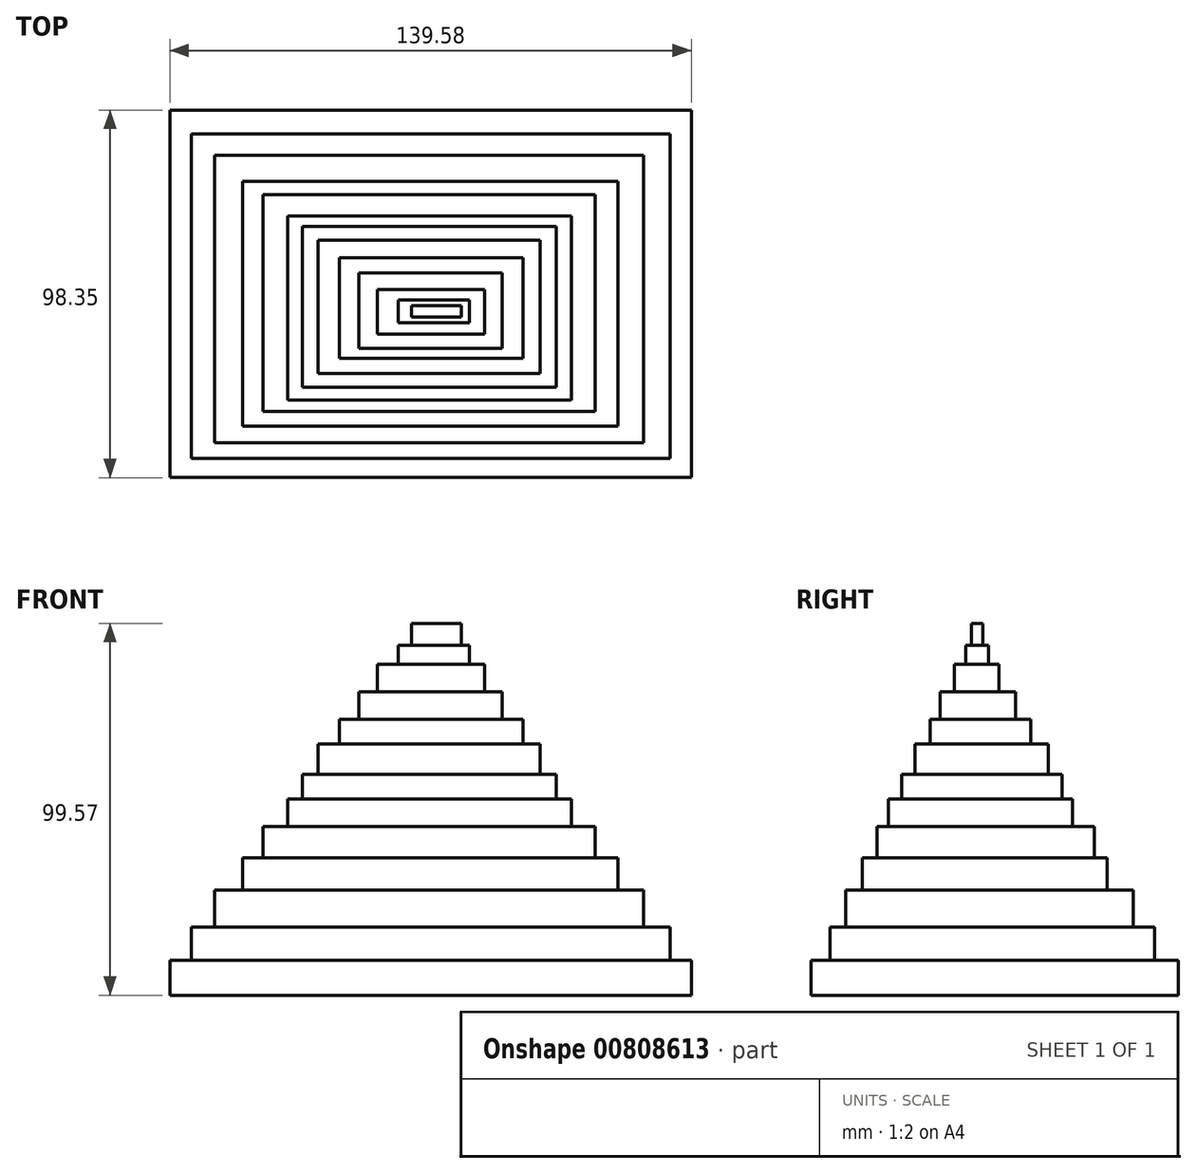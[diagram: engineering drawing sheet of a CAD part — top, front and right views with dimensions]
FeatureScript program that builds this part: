
annotation { "Feature Type Name" : "Feature", "Feature Type Description" : "" }
export const myFeature = defineFeature(function(context is Context, id is Id, definition is map)
    precondition{}
    {
        {
            var Q0;
            Q0=qCreatedBy(makeId("Top.planeOp"),FACE);
            var sketch = newSketch(context, id + "F0", { "sketchPlane" : qUnion([Q0])});
            skLineSegment(sketch, "E0.bottom", {"start": v(-69.6, 48.03) * mm, "end": v(69.98, 48.03) * mm});
            skLineSegment(sketch, "E0.top", {"start": v(-69.6, -50.32) * mm, "end": v(69.98, -50.32) * mm});
            skLineSegment(sketch, "E0.left", {"start": v(-69.6, 48.03) * mm, "end": v(-69.6, -50.32) * mm});
            skLineSegment(sketch, "E0.right", {"start": v(69.98, 48.03) * mm, "end": v(69.98, -50.32) * mm});
            skLineSegment(sketch, "E1.bottom", {"start": v(-63.87, 41.72) * mm, "end": v(64.26, 41.72) * mm});
            skLineSegment(sketch, "E1.top", {"start": v(-63.87, -45.16) * mm, "end": v(64.26, -45.16) * mm});
            skLineSegment(sketch, "E1.left", {"start": v(-63.87, 41.72) * mm, "end": v(-63.87, -45.16) * mm});
            skLineSegment(sketch, "E1.right", {"start": v(64.26, 41.72) * mm, "end": v(64.26, -45.16) * mm});
            skLineSegment(sketch, "E2.bottom", {"start": v(-57.57, 36) * mm, "end": v(57.2, 36) * mm});
            skLineSegment(sketch, "E2.top", {"start": v(-57.57, -40.96) * mm, "end": v(57.2, -40.96) * mm});
            skLineSegment(sketch, "E2.left", {"start": v(-57.57, 36) * mm, "end": v(-57.57, -40.96) * mm});
            skLineSegment(sketch, "E2.right", {"start": v(57.2, 36) * mm, "end": v(57.2, -40.96) * mm});
            skLineSegment(sketch, "E3.bottom", {"start": v(-50.13, 28.93) * mm, "end": v(50.32, 28.93) * mm});
            skLineSegment(sketch, "E3.top", {"start": v(-50.13, -36.57) * mm, "end": v(50.32, -36.57) * mm});
            skLineSegment(sketch, "E3.left", {"start": v(-50.13, 28.93) * mm, "end": v(-50.13, -36.57) * mm});
            skLineSegment(sketch, "E3.right", {"start": v(50.32, 28.93) * mm, "end": v(50.32, -36.57) * mm});
            skLineSegment(sketch, "E4.bottom", {"start": v(-44.59, 25.5) * mm, "end": v(44.2, 25.5) * mm});
            skLineSegment(sketch, "E4.top", {"start": v(-44.59, -32.56) * mm, "end": v(44.2, -32.56) * mm});
            skLineSegment(sketch, "E4.left", {"start": v(-44.59, 25.5) * mm, "end": v(-44.59, -32.56) * mm});
            skLineSegment(sketch, "E4.right", {"start": v(44.2, 25.5) * mm, "end": v(44.2, -32.56) * mm});
            skLineSegment(sketch, "E5.bottom", {"start": v(-38.1, 19.76) * mm, "end": v(37.9, 19.76) * mm});
            skLineSegment(sketch, "E5.top", {"start": v(-38.1, -29.5) * mm, "end": v(37.9, -29.5) * mm});
            skLineSegment(sketch, "E5.left", {"start": v(-38.1, 19.76) * mm, "end": v(-38.1, -29.5) * mm});
            skLineSegment(sketch, "E5.right", {"start": v(37.9, 19.76) * mm, "end": v(37.9, -29.5) * mm});
            skLineSegment(sketch, "E6.bottom", {"start": v(-34.09, 16.9) * mm, "end": v(33.9, 16.9) * mm});
            skLineSegment(sketch, "E6.top", {"start": v(-34.09, -26.07) * mm, "end": v(33.9, -26.07) * mm});
            skLineSegment(sketch, "E6.left", {"start": v(-34.09, 16.9) * mm, "end": v(-34.09, -26.07) * mm});
            skLineSegment(sketch, "E6.right", {"start": v(33.9, 16.9) * mm, "end": v(33.9, -26.07) * mm});
            skLineSegment(sketch, "E7.bottom", {"start": v(-29.88, 13.27) * mm, "end": v(29.5, 13.27) * mm});
            skLineSegment(sketch, "E7.top", {"start": v(-29.88, -22.44) * mm, "end": v(29.5, -22.44) * mm});
            skLineSegment(sketch, "E7.left", {"start": v(-29.88, 13.27) * mm, "end": v(-29.88, -22.44) * mm});
            skLineSegment(sketch, "E7.right", {"start": v(29.5, 13.27) * mm, "end": v(29.5, -22.44) * mm});
            skLineSegment(sketch, "E8.bottom", {"start": v(-24.16, 8.5) * mm, "end": v(24.92, 8.5) * mm});
            skLineSegment(sketch, "E8.top", {"start": v(-24.16, -18.43) * mm, "end": v(24.92, -18.43) * mm});
            skLineSegment(sketch, "E8.left", {"start": v(-24.16, 8.5) * mm, "end": v(-24.16, -18.43) * mm});
            skLineSegment(sketch, "E8.right", {"start": v(24.92, 8.5) * mm, "end": v(24.92, -18.43) * mm});
            skLineSegment(sketch, "E9.bottom", {"start": v(-19, 4.49) * mm, "end": v(19.38, 4.49) * mm});
            skLineSegment(sketch, "E9.top", {"start": v(-19, -15.75) * mm, "end": v(19.38, -15.75) * mm});
            skLineSegment(sketch, "E9.left", {"start": v(-19, 4.49) * mm, "end": v(-19, -15.75) * mm});
            skLineSegment(sketch, "E9.right", {"start": v(19.38, 4.49) * mm, "end": v(19.38, -15.75) * mm});
            skLineSegment(sketch, "E10.bottom", {"start": v(-14.04, 0) * mm, "end": v(14.6, 0) * mm});
            skLineSegment(sketch, "E10.top", {"start": v(-14.04, -11.93) * mm, "end": v(14.6, -11.93) * mm});
            skLineSegment(sketch, "E10.left", {"start": v(-14.04, 0) * mm, "end": v(-14.04, -11.93) * mm});
            skLineSegment(sketch, "E10.right", {"start": v(14.6, 0) * mm, "end": v(14.6, -11.93) * mm});
            skLineSegment(sketch, "E11.bottom", {"start": v(-8.5, -2.77) * mm, "end": v(10.6, -2.77) * mm});
            skLineSegment(sketch, "E11.top", {"start": v(-8.5, -8.88) * mm, "end": v(10.6, -8.88) * mm});
            skLineSegment(sketch, "E11.left", {"start": v(-8.5, -2.77) * mm, "end": v(-8.5, -8.88) * mm});
            skLineSegment(sketch, "E11.right", {"start": v(10.6, -2.77) * mm, "end": v(10.6, -8.88) * mm});
            skLineSegment(sketch, "E12.bottom", {"start": v(-4.87, -4.3) * mm, "end": v(8.5, -4.3) * mm});
            skLineSegment(sketch, "E12.top", {"start": v(-4.87, -7.35) * mm, "end": v(8.5, -7.35) * mm});
            skLineSegment(sketch, "E12.left", {"start": v(-4.87, -4.3) * mm, "end": v(-4.87, -7.35) * mm});
            skLineSegment(sketch, "E12.right", {"start": v(8.5, -4.3) * mm, "end": v(8.5, -7.35) * mm});
            skPoint(sketch, "E13.oppositeSnap0", {"position": v(8.5, -5.82) * mm});
            skLineSegment(sketch, "E13.bottom", {"start": v(-2.77, -5.82) * mm, "end": v(5.44, -5.82) * mm});
            skLineSegment(sketch, "E13.top", {"start": v(-2.77, -5.82) * mm, "end": v(5.44, -5.82) * mm});
            skLineSegment(sketch, "E13.left", {"start": v(-2.77, -5.82) * mm, "end": v(-2.77, -5.82) * mm});
            skLineSegment(sketch, "E13.right", {"start": v(5.44, -5.82) * mm, "end": v(5.44, -5.82) * mm});
            skSolve(sketch);
        }
        {
            var Q0;
            Q0=makeQuery(id+"F0.imprint","IMPRINT",FACE,{"disambiguationData":[TD([[makeQuery(id+"F0.imprint","IMPRINT",EDGE,{"derivedFrom":sQuery(id+"F0.wireOp",EDGE,"E12.bottom")}),-1.0]])]});
            extrude(context, id + "F1", {"entities" : qUnion([Q0]), "depth" : 99.57 * mm, "offsetDistance" : 25.4 * mm});
        }
        {
            var Q0;
            Q0=makeQuery(id+"F0.imprint","IMPRINT",FACE,{"disambiguationData":[TD([[makeQuery(id+"F0.imprint","IMPRINT",EDGE,{"derivedFrom":sQuery(id+"F0.wireOp",EDGE,"E11.bottom")}),-1.0]])]});
            extrude(context, id + "F2", {"entities" : qUnion([Q0]), "operationType" : NewBodyOperationType.ADD, "depth" : 93.73 * mm, "offsetDistance" : 25.4 * mm});
        }
        {
            var Q0;
            Q0=makeQuery(id+"F0.imprint","IMPRINT",FACE,{"disambiguationData":[TD([[makeQuery(id+"F0.imprint","IMPRINT",EDGE,{"derivedFrom":sQuery(id+"F0.wireOp",EDGE,"E10.bottom")}),-1.0]])]});
            extrude(context, id + "F3", {"entities" : qUnion([Q0]), "operationType" : NewBodyOperationType.ADD, "depth" : 88.65 * mm, "offsetDistance" : 25.4 * mm});
        }
        {
            var Q0;
            Q0=makeQuery(id+"F0.imprint","IMPRINT",FACE,{"disambiguationData":[TD([[makeQuery(id+"F0.imprint","IMPRINT",EDGE,{"derivedFrom":sQuery(id+"F0.wireOp",EDGE,"E9.bottom")}),-1.0]])]});
            extrude(context, id + "F4", {"entities" : qUnion([Q0]), "operationType" : NewBodyOperationType.ADD, "depth" : 81.28 * mm, "offsetDistance" : 25.4 * mm});
        }
        {
            var Q0;
            Q0=makeQuery(id+"F0.imprint","IMPRINT",FACE,{"disambiguationData":[TD([[makeQuery(id+"F0.imprint","IMPRINT",EDGE,{"derivedFrom":sQuery(id+"F0.wireOp",EDGE,"E8.bottom")}),-1.0]])]});
            extrude(context, id + "F5", {"entities" : qUnion([Q0]), "operationType" : NewBodyOperationType.ADD, "depth" : 73.9 * mm, "offsetDistance" : 25.4 * mm});
        }
        {
            var Q0;
            Q0=makeQuery(id+"F0.imprint","IMPRINT",FACE,{"disambiguationData":[TD([[makeQuery(id+"F0.imprint","IMPRINT",EDGE,{"derivedFrom":sQuery(id+"F0.wireOp",EDGE,"E7.bottom")}),-1.0]])]});
            extrude(context, id + "F6", {"entities" : qUnion([Q0]), "operationType" : NewBodyOperationType.ADD, "depth" : 67.3 * mm, "offsetDistance" : 25.4 * mm});
        }
        {
            var Q0;
            Q0=makeQuery(id+"F0.imprint","IMPRINT",FACE,{"disambiguationData":[TD([[makeQuery(id+"F0.imprint","IMPRINT",EDGE,{"derivedFrom":sQuery(id+"F0.wireOp",EDGE,"E6.bottom")}),-1.0]])]});
            extrude(context, id + "F7", {"entities" : qUnion([Q0]), "operationType" : NewBodyOperationType.ADD, "depth" : 59.18 * mm, "offsetDistance" : 25.4 * mm});
        }
        {
            var Q0;
            Q0=makeQuery(id+"F0.imprint","IMPRINT",FACE,{"disambiguationData":[TD([[makeQuery(id+"F0.imprint","IMPRINT",EDGE,{"derivedFrom":sQuery(id+"F0.wireOp",EDGE,"E5.bottom")}),-1.0]])]});
            extrude(context, id + "F8", {"entities" : qUnion([Q0]), "operationType" : NewBodyOperationType.ADD, "depth" : 52.58 * mm, "offsetDistance" : 25.4 * mm});
        }
        {
            var Q0;
            Q0=makeQuery(id+"F0.imprint","IMPRINT",FACE,{"disambiguationData":[TD([[makeQuery(id+"F0.imprint","IMPRINT",EDGE,{"derivedFrom":sQuery(id+"F0.wireOp",EDGE,"E4.bottom")}),-1.0]])]});
            extrude(context, id + "F9", {"entities" : qUnion([Q0]), "operationType" : NewBodyOperationType.ADD, "depth" : 45.2 * mm, "offsetDistance" : 25.4 * mm});
        }
        {
            var Q0;
            Q0=makeQuery(id+"F0.imprint","IMPRINT",FACE,{"disambiguationData":[TD([[makeQuery(id+"F0.imprint","IMPRINT",EDGE,{"derivedFrom":sQuery(id+"F0.wireOp",EDGE,"E3.bottom")}),-1.0]])]});
            extrude(context, id + "F10", {"entities" : qUnion([Q0]), "operationType" : NewBodyOperationType.ADD, "depth" : 36.83 * mm, "offsetDistance" : 25.4 * mm});
        }
        {
            var Q0;
            Q0=makeQuery(id+"F0.imprint","IMPRINT",FACE,{"disambiguationData":[TD([[makeQuery(id+"F0.imprint","IMPRINT",EDGE,{"derivedFrom":sQuery(id+"F0.wireOp",EDGE,"E2.bottom")}),-1.0]])]});
            extrude(context, id + "F11", {"entities" : qUnion([Q0]), "operationType" : NewBodyOperationType.ADD, "depth" : 28.2 * mm, "offsetDistance" : 25.4 * mm});
        }
        {
            var Q0;
            Q0=makeQuery(id+"F0.imprint","IMPRINT",FACE,{"disambiguationData":[TD([[makeQuery(id+"F0.imprint","IMPRINT",EDGE,{"derivedFrom":sQuery(id+"F0.wireOp",EDGE,"E1.bottom")}),-1.0]])]});
            extrude(context, id + "F12", {"entities" : qUnion([Q0]), "operationType" : NewBodyOperationType.ADD, "depth" : 18.29 * mm, "offsetDistance" : 25.4 * mm});
        }
        {
            var Q0;
            Q0 = qSketchRegion(id + "F0", true);
            extrude(context, id + "F13", {"entities" : qUnion([Q0]), "operationType" : NewBodyOperationType.ADD, "depth" : 9.4 * mm, "offsetDistance" : 25.4 * mm});
        }
        {
            var Q0;
            Q0=sQuery(id+"F0.wireOp",EDGE,"E13.top");
            extrude(context, id + "F14", {"bodyType" : ToolBodyType.SURFACE, "surfaceEntities" : qUnion([Q0]), "depth" : 104.9 * mm, "offsetDistance" : 25.4 * mm});
        }
    });
